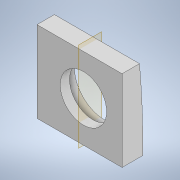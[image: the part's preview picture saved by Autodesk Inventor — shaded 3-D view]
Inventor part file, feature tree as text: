
AUTODESK INVENTOR PART (.ipt)
format: ipt  version: 2021.1 (Build 251245000, 245)  size: 705,536 bytes
history: native  units: in
note: dims shown in document units (in); Inventor stores cm internally (conversion verified against a paired STEP export)
features: extrude x4, sketch x4, plane x1, emboss x1, split x1
ambient origin geometry x8: Origin, YZ Plane, XZ Plane, XY Plane, X Axis, Y Axis, Z Axis, Center Point
bodies: Solid1 (feature_tree)
feature tree (11):
  extrude  "Extrusion1"  Depth=4.0in
  extrude  "Extrusion2"  Depth=22.0in
  plane  "Work Plane2"
  extrude  "Extrusion3"  Depth=22.0in
  emboss  "Emboss1"
  extrude  "Extrusion4"  TaperAngle=0.0deg  [1 undecoded]
  split  "Split1"
  sketch  "Sketch1"  dims[d0=0.5in d1=4.0in]
  sketch  "Sketch3"  dims[d5=22.0in d6=4.0in]
  sketch  "Sketch4"  dims[d7=22.0in d8=2.1in]
  sketch  "Sketch5"  dims[d9=2.2in d10=0.0in d11=1.2in d12=1.05in d13=0.0in d14=0.0in d15=0.15in d16=0.3in d17=0.0in d18=0.175in d19=0.05in d20=0.0in d22=1.2in d23=0.05in d24=0.0in d25=0.0in]
note: 1 required parameter value undecoded (feature->parameter linkage not recoverable at this tier; creation-order binding heuristic only, values carry confidence <= 0.55)
